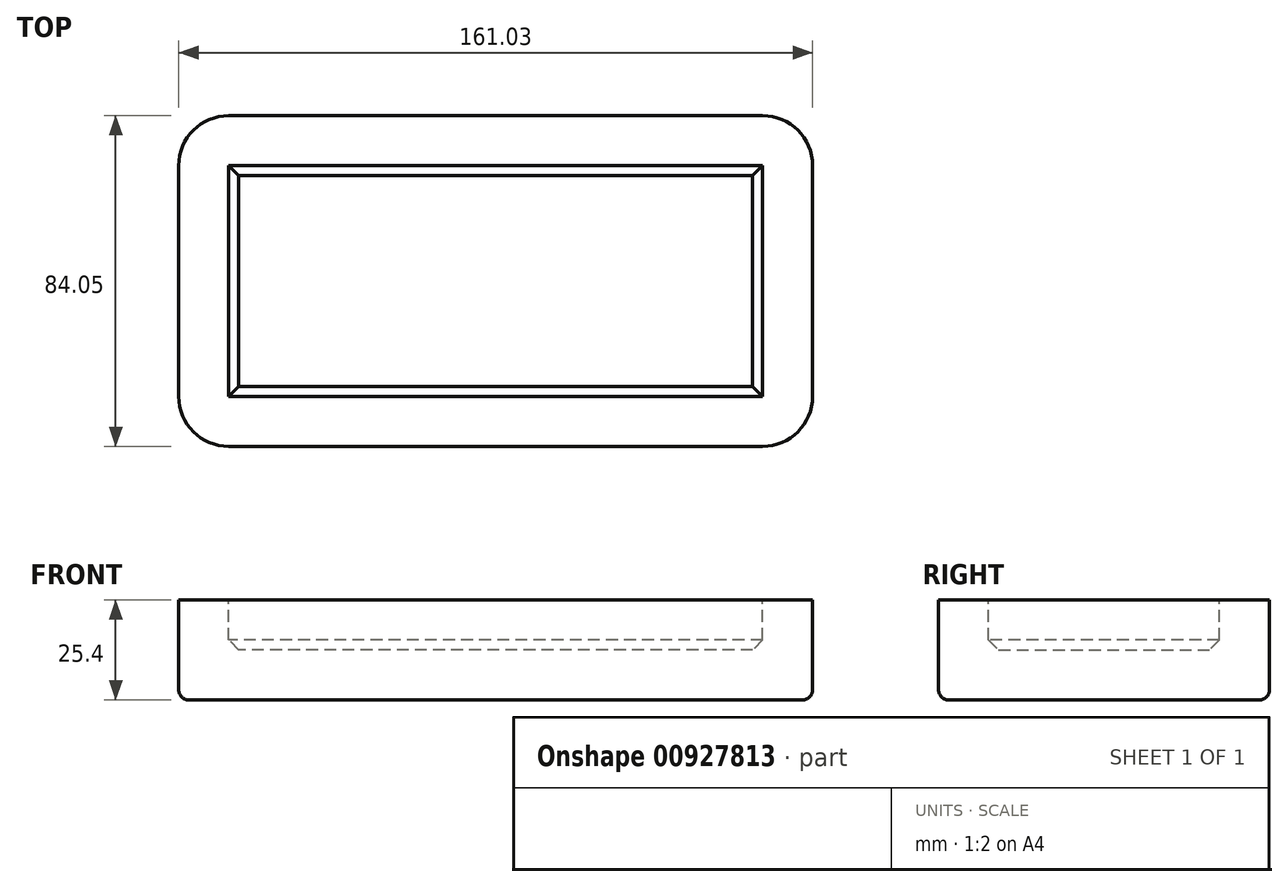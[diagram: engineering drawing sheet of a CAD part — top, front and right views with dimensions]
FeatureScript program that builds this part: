
annotation { "Feature Type Name" : "Feature", "Feature Type Description" : "" }
export const myFeature = defineFeature(function(context is Context, id is Id, definition is map)
    precondition{}
    {
        {
            var Q0;
            Q0=qCreatedBy(makeId("Top.planeOp"),FACE);
            var sketch = newSketch(context, id + "F0", { "sketchPlane" : qUnion([Q0])});
            skLineSegment(sketch, "E0", {"start": v(-148.33, 0) * mm, "end": v(-12.7, 0) * mm});
            skLineSegment(sketch, "E1", {"start": v(0, -12.7) * mm, "end": v(0, -71.35) * mm});
            skLineSegment(sketch, "E2", {"start": v(-12.7, -84.05) * mm, "end": v(-148.33, -84.05) * mm});
            skLineSegment(sketch, "E3", {"start": v(-161.03, -71.35) * mm, "end": v(-161.03, -12.7) * mm});
            skPoint(sketch, "E4.visualSharp", {"position": v(-161.03, -84.05) * mm});
            skArc(sketch, "E4.filletArc", {"start": v(-161.03, -71.35) * mm, "mid": v(-157.3, -80.33) * mm, "end": v(-148.33, -84.05) * mm});
            skPoint(sketch, "E5.visualSharp", {"position": v(-161.03, 0) * mm});
            skArc(sketch, "E5.filletArc", {"start": v(-148.33, 0) * mm, "mid": v(-157.3, -3.72) * mm, "end": v(-161.03, -12.7) * mm});
            skPoint(sketch, "E6.visualSharp", {"position": v(0, 0) * mm});
            skArc(sketch, "E6.filletArc", {"start": v(0, -12.7) * mm, "mid": v(-3.72, -3.72) * mm, "end": v(-12.7, 0) * mm});
            skPoint(sketch, "E7.visualSharp", {"position": v(0, -84.05) * mm});
            skArc(sketch, "E7.filletArc", {"start": v(-12.7, -84.05) * mm, "mid": v(-3.72, -80.33) * mm, "end": v(0, -71.35) * mm});
            skSolve(sketch);
        }
        {
            var Q0;
            Q0=makeQuery(id+"F0.imprint","IMPRINT",FACE,{"disambiguationData":[TD([[makeQuery(id+"F0.imprint","IMPRINT",EDGE,{"derivedFrom":sQuery(id+"F0.wireOp",EDGE,"E0")}),-1.0]])]});
            extrude(context, id + "F1", {"entities" : qUnion([Q0]), "depth" : 25.4 * mm, "offsetDistance" : 25.4 * mm});
        }
        {
            var Q0;
            Q0=makeQuery(id+"F1.opExtrude","CAP_FACE",FACE,{"disambiguationData":[OSD([sQuery(id+"F0.wireOp",EDGE,"E0"),sQuery(id+"F0.wireOp",EDGE,"E1"),sQuery(id+"F0.wireOp",EDGE,"E2"),sQuery(id+"F0.wireOp",EDGE,"E3"),sQuery(id+"F0.wireOp",EDGE,"E4.filletArc"),sQuery(id+"F0.wireOp",EDGE,"E5.filletArc"),sQuery(id+"F0.wireOp",EDGE,"E6.filletArc"),sQuery(id+"F0.wireOp",EDGE,"E7.filletArc")])],"isStart":false});
            var sketch = newSketch(context, id + "F2", { "sketchPlane" : qUnion([Q0])});
            skLineSegment(sketch, "E8", {"start": v(-148.33, -12.7) * mm, "end": v(-148.33, -71.35) * mm});
            skLineSegment(sketch, "E9", {"start": v(-12.7, -12.7) * mm, "end": v(-12.7, -71.35) * mm});
            skLineSegment(sketch, "E10", {"start": v(-12.7, -71.35) * mm, "end": v(-148.33, -71.35) * mm});
            skLineSegment(sketch, "E11", {"start": v(-148.33, -12.7) * mm, "end": v(-12.7, -12.7) * mm});
            skSolve(sketch);
        }
        {
            var Q0;
            Q0 = qSketchRegion(id + "F2", true);
            extrude(context, id + "F3", {"entities" : qUnion([Q0]), "operationType" : NewBodyOperationType.REMOVE, "oppositeDirection" : true, "depth" : 12.7 * mm, "offsetDistance" : 25.4 * mm});
        }
        {
            var Q0;
            Q0=makeQuery(id+"F3.boolean.opBoolean","COPY",EDGE,{"derivedFrom":makeQuery(id+"F3.opExtrude","CAP_EDGE",EDGE,{"disambiguationData":[OSD([sQuery(id+"F2.wireOp",EDGE,"E11")])],"isStart":true})});
            var Q1;
            Q1=makeQuery(id+"F1.opExtrude","CAP_FACE",FACE,{"disambiguationData":[OSD([sQuery(id+"F0.wireOp",EDGE,"E0"),sQuery(id+"F0.wireOp",EDGE,"E1"),sQuery(id+"F0.wireOp",EDGE,"E2"),sQuery(id+"F0.wireOp",EDGE,"E3"),sQuery(id+"F0.wireOp",EDGE,"E4.filletArc"),sQuery(id+"F0.wireOp",EDGE,"E5.filletArc"),sQuery(id+"F0.wireOp",EDGE,"E6.filletArc"),sQuery(id+"F0.wireOp",EDGE,"E7.filletArc")])],"isStart":true});
            fillet(context, id + "F4", {"entities" : qUnion([Q0, Q1]), "radius" : 2.54 * mm, "tangentPropagation" : true, "allowEdgeOverflow" : false});
        }
        {
            var Q0;
            Q0=makeQuery(id+"F3.boolean.opBoolean","COPY",FACE,{"derivedFrom":makeQuery(id+"F3.opExtrude","CAP_FACE",FACE,{"disambiguationData":[OSD([sQuery(id+"F2.wireOp",EDGE,"E8"),sQuery(id+"F2.wireOp",EDGE,"E9"),sQuery(id+"F2.wireOp",EDGE,"E10"),sQuery(id+"F2.wireOp",EDGE,"E11")])],"isStart":false})});
            var Q1;
            Q1=makeQuery(id+"F4.opFillet","BLEND_EDGE",EDGE,{"blendedFrom":[makeQuery(id+"F3.boolean.opBoolean","COPY",EDGE,{"derivedFrom":makeQuery(id+"F3.opExtrude","CAP_EDGE",EDGE,{"disambiguationData":[OSD([sQuery(id+"F2.wireOp",EDGE,"E11")])],"isStart":true})}),makeQuery(id+"F1.opExtrude","CAP_FACE",FACE,{"disambiguationData":[OSD([sQuery(id+"F0.wireOp",EDGE,"E0"),sQuery(id+"F0.wireOp",EDGE,"E1"),sQuery(id+"F0.wireOp",EDGE,"E2"),sQuery(id+"F0.wireOp",EDGE,"E3"),sQuery(id+"F0.wireOp",EDGE,"E4.filletArc"),sQuery(id+"F0.wireOp",EDGE,"E5.filletArc"),sQuery(id+"F0.wireOp",EDGE,"E6.filletArc"),sQuery(id+"F0.wireOp",EDGE,"E7.filletArc")])],"isStart":false})],"blendedInto":[makeQuery(id+"F1.opExtrude","CAP_FACE",FACE,{"disambiguationData":[OSD([sQuery(id+"F0.wireOp",EDGE,"E0"),sQuery(id+"F0.wireOp",EDGE,"E1"),sQuery(id+"F0.wireOp",EDGE,"E2"),sQuery(id+"F0.wireOp",EDGE,"E3"),sQuery(id+"F0.wireOp",EDGE,"E4.filletArc"),sQuery(id+"F0.wireOp",EDGE,"E5.filletArc"),sQuery(id+"F0.wireOp",EDGE,"E6.filletArc"),sQuery(id+"F0.wireOp",EDGE,"E7.filletArc")])],"isStart":false})]});
            var Q2;
            Q2=makeQuery(id+"F3.boolean.opBoolean","COPY",EDGE,{"derivedFrom":makeQuery(id+"F3.opExtrude","CAP_EDGE",EDGE,{"disambiguationData":[OSD([sQuery(id+"F2.wireOp",EDGE,"E8")])],"isStart":true})});
            var Q3;
            Q3=makeQuery(id+"F3.boolean.opBoolean","COPY",EDGE,{"derivedFrom":makeQuery(id+"F3.opExtrude","CAP_EDGE",EDGE,{"disambiguationData":[OSD([sQuery(id+"F2.wireOp",EDGE,"E10")])],"isStart":true})});
            var Q4;
            Q4=makeQuery(id+"F3.boolean.opBoolean","COPY",EDGE,{"derivedFrom":makeQuery(id+"F3.opExtrude","CAP_EDGE",EDGE,{"disambiguationData":[OSD([sQuery(id+"F2.wireOp",EDGE,"E9")])],"isStart":true})});
            chamfer(context, id + "F5", {"entities" : qUnion([Q0, Q1, Q2, Q3, Q4]), "width" : 2.54 * mm, "tangentPropagation" : true});
        }
    });
